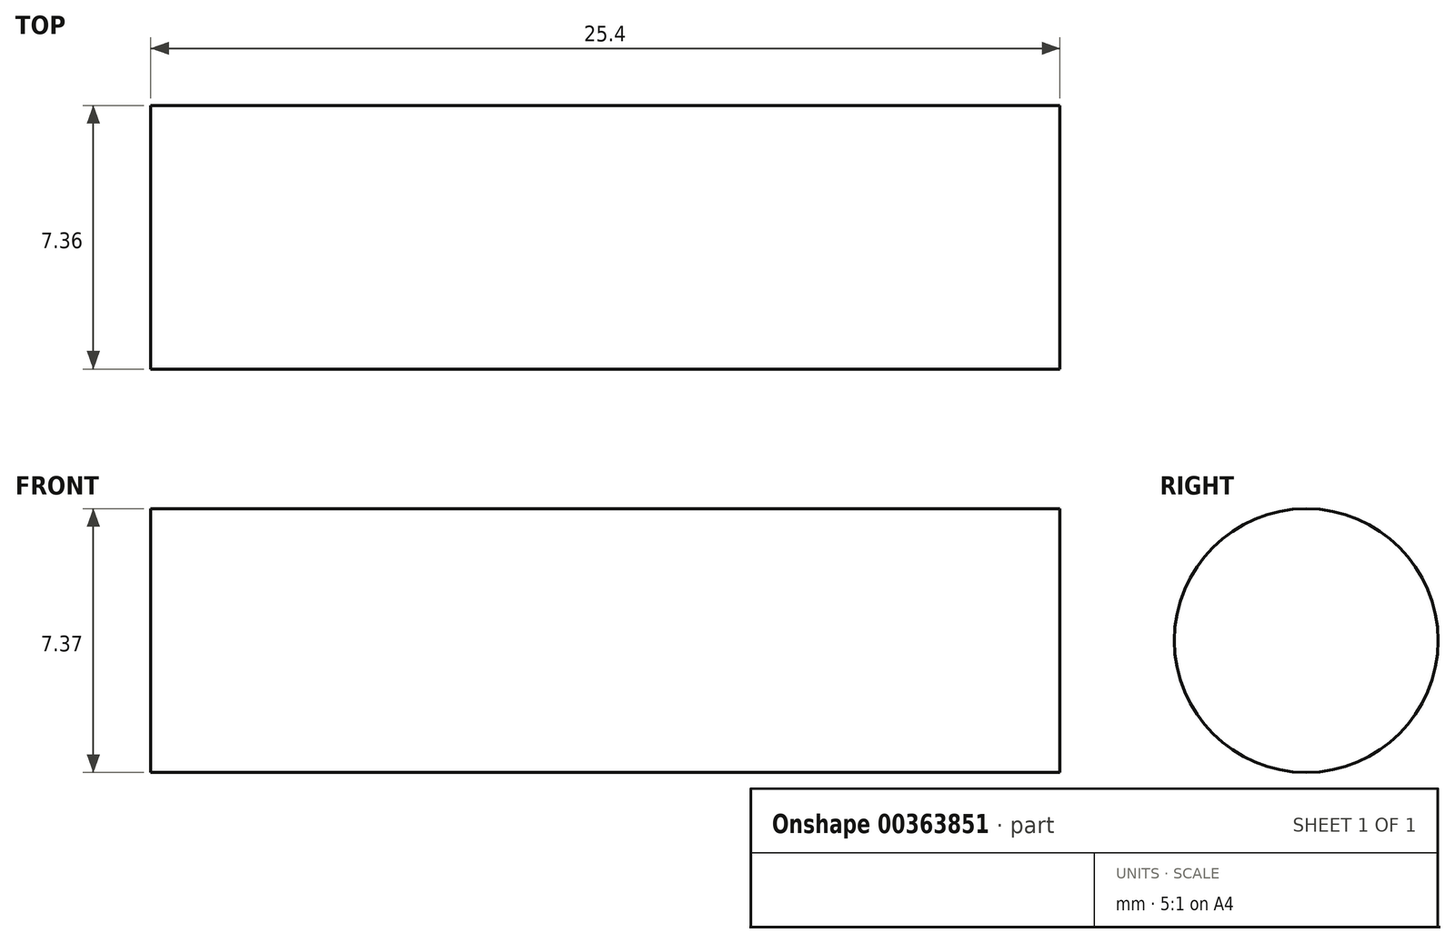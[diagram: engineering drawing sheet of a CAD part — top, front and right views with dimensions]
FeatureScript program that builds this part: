
annotation { "Feature Type Name" : "Feature", "Feature Type Description" : "" }
export const myFeature = defineFeature(function(context is Context, id is Id, definition is map)
    precondition{}
    {
        {
            var Q0;
            Q0=qCreatedBy(makeId("Right.planeOp"),FACE);
            var sketch = newSketch(context, id + "F0", { "sketchPlane" : qUnion([Q0])});
            skCircle(sketch, "E0", {"center": v(-36.35, 22.96) * mm, "radius": 3.68 * mm});
            skSolve(sketch);
        }
        {
            var Q0;
            Q0=makeQuery(id+"F0.imprint","IMPRINT",FACE,{"disambiguationData":[TD([[makeQuery(id+"F0.imprint","IMPRINT",EDGE,{"derivedFrom":sQuery(id+"F0.wireOp",EDGE,"E0")}),1.0]])]});
            extrude(context, id + "F1", {"entities" : qUnion([Q0]), "depth" : 25.4 * mm});
        }
    });
